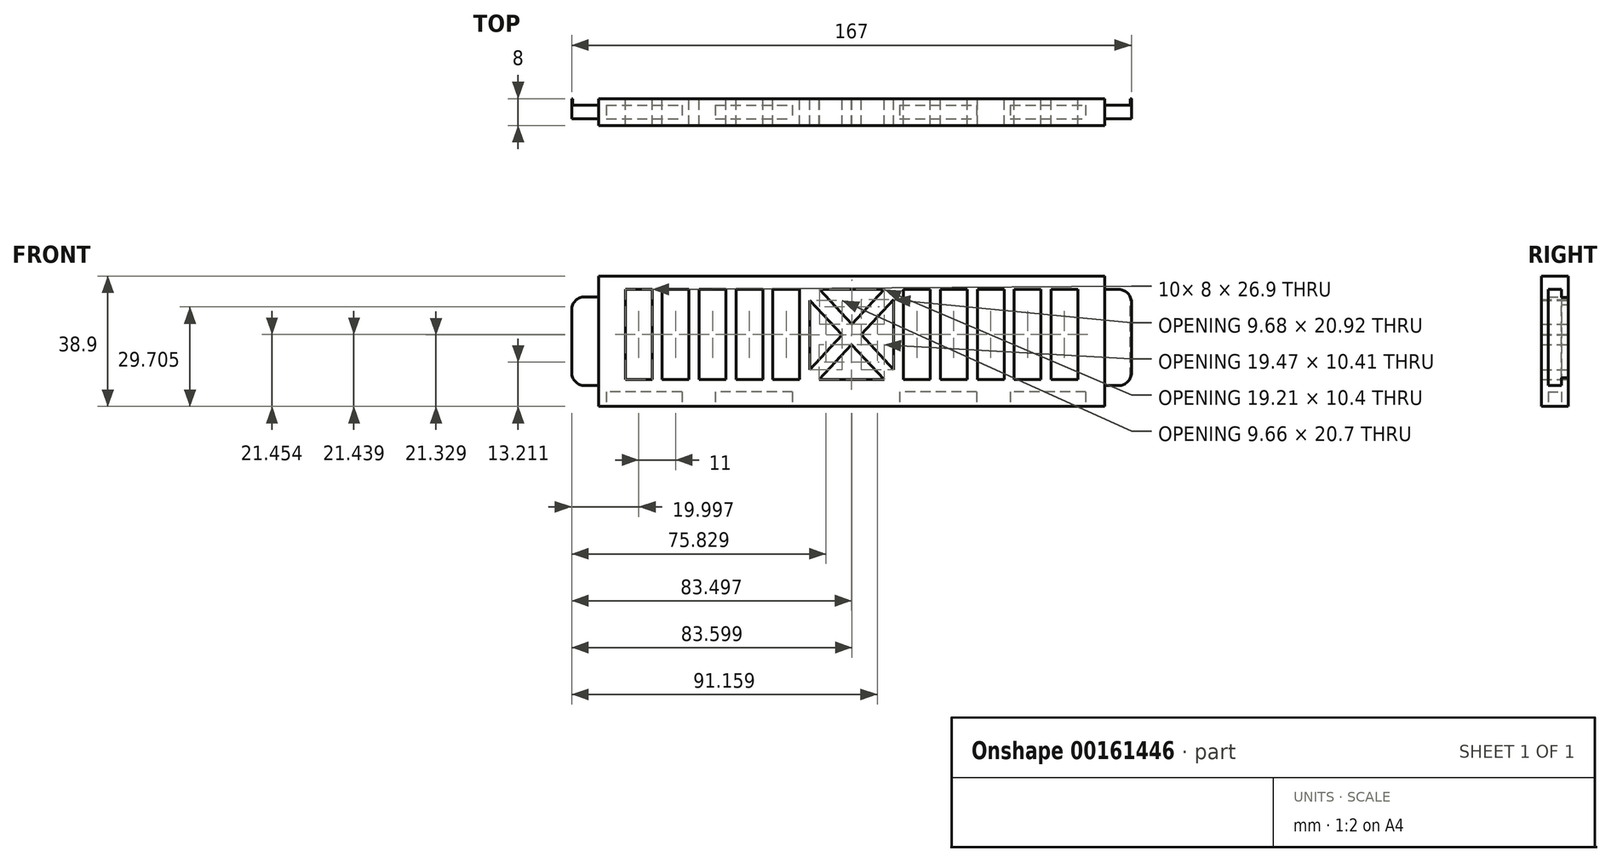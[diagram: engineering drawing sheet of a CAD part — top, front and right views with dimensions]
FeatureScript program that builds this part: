
annotation { "Feature Type Name" : "Feature", "Feature Type Description" : "" }
export const myFeature = defineFeature(function(context is Context, id is Id, definition is map)
    precondition{}
    {
        {
            var Q0;
            Q0=qCreatedBy(makeId("Front.planeOp"),FACE);
            var sketch = newSketch(context, id + "F0", { "sketchPlane" : qUnion([Q0])});
            skLineSegment(sketch, "E0.bottom", {"start": v(-77.72, 39.57) * mm, "end": v(73.28, 39.57) * mm});
            skLineSegment(sketch, "E0.top", {"start": v(-77.72, 0.67) * mm, "end": v(73.28, 0.67) * mm});
            skLineSegment(sketch, "E0.left", {"start": v(-77.72, 39.57) * mm, "end": v(-77.72, 0.67) * mm});
            skLineSegment(sketch, "E0.right", {"start": v(73.28, 39.57) * mm, "end": v(73.28, 0.67) * mm});
            skLineSegment(sketch, "E1.left", {"start": v(-77.72, 0.67) * mm, "end": v(-77.72, 15.56) * mm});
            skLineSegment(sketch, "E1.right", {"start": v(-85.72, 10.7) * mm, "end": v(-85.72, 29.54) * mm});
            skLineSegment(sketch, "E2.left", {"start": v(73.28, 39.57) * mm, "end": v(73.28, -23.35) * mm});
            skLineSegment(sketch, "E3.top", {"start": v(-77.72, 6.87) * mm, "end": v(-81.89, 6.87) * mm});
            skLineSegment(sketch, "E3.left", {"start": v(-77.72, 0.67) * mm, "end": v(-77.72, 6.87) * mm});
            skLineSegment(sketch, "E4.top", {"start": v(-81.89, 33.37) * mm, "end": v(-77.72, 33.37) * mm});
            skLineSegment(sketch, "E4.right", {"start": v(-77.72, 33.37) * mm, "end": v(-77.72, 15.56) * mm});
            skLineSegment(sketch, "E5.bottom", {"start": v(73.28, 6.87) * mm, "end": v(77.44, 6.87) * mm});
            skLineSegment(sketch, "E5.top", {"start": v(73.28, 35.57) * mm, "end": v(77.44, 35.57) * mm});
            skLineSegment(sketch, "E5.left", {"start": v(73.28, 6.87) * mm, "end": v(73.28, 35.57) * mm});
            skLineSegment(sketch, "E5.right", {"start": v(81.28, 10.7) * mm, "end": v(81.28, 31.74) * mm});
            skArc(sketch, "E6.filletArc", {"start": v(81.28, 31.74) * mm, "mid": v(80.15, 34.45) * mm, "end": v(77.44, 35.57) * mm});
            skPoint(sketch, "E7.visualSharp", {"position": v(81.28, 6.87) * mm});
            skArc(sketch, "E7.filletArc", {"start": v(77.44, 6.87) * mm, "mid": v(80.15, 8) * mm, "end": v(81.28, 10.7) * mm});
            skArc(sketch, "E8.filletArc", {"start": v(-81.89, 33.37) * mm, "mid": v(-84.6, 32.25) * mm, "end": v(-85.72, 29.54) * mm});
            skPoint(sketch, "E9.visualSharp", {"position": v(-85.72, 6.87) * mm});
            skArc(sketch, "E9.filletArc", {"start": v(-85.72, 10.7) * mm, "mid": v(-84.6, 8) * mm, "end": v(-81.89, 6.87) * mm});
            skLineSegment(sketch, "E10.bottom", {"start": v(-77.72, 39.57) * mm, "end": v(-69.72, 39.57) * mm});
            skLineSegment(sketch, "E10.top", {"start": v(-77.72, 0.67) * mm, "end": v(-69.72, 0.67) * mm});
            skLineSegment(sketch, "E10.right", {"start": v(-69.72, 35.57) * mm, "end": v(-69.72, 8.67) * mm});
            skLineSegment(sketch, "E11.bottom", {"start": v(73.28, 39.57) * mm, "end": v(65.28, 39.57) * mm});
            skLineSegment(sketch, "E11.top", {"start": v(73.28, 0.67) * mm, "end": v(65.28, 0.67) * mm});
            skLineSegment(sketch, "E11.right", {"start": v(65.28, 35.57) * mm, "end": v(65.28, 8.67) * mm});
            skLineSegment(sketch, "E12.bottom", {"start": v(-69.72, 8.67) * mm, "end": v(-61.72, 8.67) * mm});
            skLineSegment(sketch, "E12.left", {"start": v(-77.72, 8.67) * mm, "end": v(-77.72, 0.67) * mm});
            skLineSegment(sketch, "E12.right", {"start": v(73.28, 8.67) * mm, "end": v(73.28, 0.67) * mm});
            skLineSegment(sketch, "E13.top", {"start": v(-69.72, 35.57) * mm, "end": v(-61.72, 35.57) * mm});
            skLineSegment(sketch, "E13.left", {"start": v(-77.72, 39.57) * mm, "end": v(-77.72, 35.57) * mm});
            skLineSegment(sketch, "E13.right", {"start": v(73.28, 39.57) * mm, "end": v(73.28, 35.57) * mm});
            skLineSegment(sketch, "E14", {"start": v(-61.72, 35.57) * mm, "end": v(-61.72, 8.67) * mm});
            skLineSegment(sketch, "E15", {"start": v(-58.72, 35.57) * mm, "end": v(-58.72, 8.67) * mm});
            skLineSegment(sketch, "E16", {"start": v(-50.72, 35.57) * mm, "end": v(-50.72, 8.67) * mm});
            skLineSegment(sketch, "E17", {"start": v(-47.72, 35.57) * mm, "end": v(-47.72, 8.67) * mm});
            skLineSegment(sketch, "E18", {"start": v(-39.72, 35.57) * mm, "end": v(-39.72, 8.67) * mm});
            skLineSegment(sketch, "E19.bottom", {"start": v(-36.72, 35.57) * mm, "end": v(-28.72, 35.57) * mm});
            skLineSegment(sketch, "E19.top", {"start": v(-36.72, 8.67) * mm, "end": v(-28.72, 8.67) * mm});
            skLineSegment(sketch, "E19.left", {"start": v(-36.72, 35.57) * mm, "end": v(-36.72, 8.67) * mm});
            skLineSegment(sketch, "E19.right", {"start": v(-28.72, 35.57) * mm, "end": v(-28.72, 8.67) * mm});
            skLineSegment(sketch, "E20.bottom", {"start": v(-25.72, 35.57) * mm, "end": v(-17.72, 35.57) * mm});
            skLineSegment(sketch, "E20.top", {"start": v(-25.72, 8.67) * mm, "end": v(-17.72, 8.67) * mm});
            skLineSegment(sketch, "E20.left", {"start": v(-25.72, 35.57) * mm, "end": v(-25.72, 8.67) * mm});
            skLineSegment(sketch, "E20.right", {"start": v(-17.72, 35.57) * mm, "end": v(-17.72, 8.67) * mm});
            skLineSegment(sketch, "E21.left", {"start": v(-14.72, 32.35) * mm, "end": v(-14.72, 11.65) * mm});
            skLineSegment(sketch, "E22.left", {"start": v(10.28, 32.57) * mm, "end": v(10.28, 11.65) * mm});
            skLineSegment(sketch, "E22.right", {"start": v(13.28, 35.57) * mm, "end": v(13.28, 8.67) * mm});
            skLineSegment(sketch, "E23.left", {"start": v(21.28, 35.57) * mm, "end": v(21.28, 8.67) * mm});
            skLineSegment(sketch, "E23.right", {"start": v(24.28, 35.57) * mm, "end": v(24.28, 8.67) * mm});
            skLineSegment(sketch, "E24.bottom", {"start": v(32.28, 35.57) * mm, "end": v(35.28, 35.57) * mm});
            skLineSegment(sketch, "E24.left", {"start": v(32.28, 35.57) * mm, "end": v(32.28, 8.67) * mm});
            skLineSegment(sketch, "E24.right", {"start": v(35.28, 35.57) * mm, "end": v(35.28, 8.67) * mm});
            skLineSegment(sketch, "E25.left", {"start": v(43.28, 35.57) * mm, "end": v(43.28, 8.67) * mm});
            skLineSegment(sketch, "E25.right", {"start": v(46.28, 35.57) * mm, "end": v(46.28, 8.67) * mm});
            skLineSegment(sketch, "E26.left", {"start": v(54.28, 35.57) * mm, "end": v(54.28, 8.67) * mm});
            skLineSegment(sketch, "E26.right", {"start": v(57.28, 35.57) * mm, "end": v(57.28, 8.67) * mm});
            skLineSegment(sketch, "E27.right", {"start": v(73.28, 11.56) * mm, "end": v(73.28, 8.67) * mm});
            skPoint(sketch, "E28.start.orphan", {"position": v(65.28, 24.02) * mm});
            skLineSegment(sketch, "E29", {"start": v(10.28, 32.57) * mm, "end": v(0.6, 22.17) * mm});
            skLineSegment(sketch, "E30", {"start": v(-14.72, 11.65) * mm, "end": v(-5.06, 22.06) * mm});
            skLineSegment(sketch, "E31", {"start": v(10.28, 11.65) * mm, "end": v(0.6, 22.17) * mm});
            skLineSegment(sketch, "E32", {"start": v(-14.72, 32.35) * mm, "end": v(-5.06, 22.06) * mm});
            skLineSegment(sketch, "E33.trimOffspring", {"start": v(13.28, 35.57) * mm, "end": v(21.28, 35.57) * mm});
            skLineSegment(sketch, "E34.trimOffspring", {"start": v(-2.17, 25.18) * mm, "end": v(-11.73, 35.57) * mm});
            skLineSegment(sketch, "E35.trimOffspring", {"start": v(-2.27, 19.09) * mm, "end": v(-11.96, 8.67) * mm});
            skLineSegment(sketch, "E36.trimOffspring", {"start": v(-2.17, 25.18) * mm, "end": v(7.48, 35.57) * mm});
            skLineSegment(sketch, "E37.trimOffspring", {"start": v(-2.27, 19.09) * mm, "end": v(7.51, 8.67) * mm});
            skLineSegment(sketch, "E38.trimOffspring", {"start": v(13.28, 8.67) * mm, "end": v(21.28, 8.67) * mm});
            skLineSegment(sketch, "E39.trimOffspring", {"start": v(24.28, 8.67) * mm, "end": v(32.28, 8.67) * mm});
            skLineSegment(sketch, "E40.trimOffspring", {"start": v(35.28, 8.67) * mm, "end": v(43.28, 8.67) * mm});
            skLineSegment(sketch, "E41.trimOffspring", {"start": v(57.28, 8.67) * mm, "end": v(65.28, 8.67) * mm});
            skLineSegment(sketch, "E42.trimOffspring", {"start": v(24.28, 35.57) * mm, "end": v(32.28, 35.57) * mm});
            skLineSegment(sketch, "E43.trimOffspring", {"start": v(35.28, 35.57) * mm, "end": v(43.28, 35.57) * mm});
            skLineSegment(sketch, "E44.trimOffspring", {"start": v(46.28, 35.57) * mm, "end": v(54.28, 35.57) * mm});
            skLineSegment(sketch, "E45.trimOffspring", {"start": v(-47.72, 35.57) * mm, "end": v(-39.72, 35.57) * mm});
            skLineSegment(sketch, "E46.trimOffspring", {"start": v(-58.72, 8.67) * mm, "end": v(-50.72, 8.67) * mm});
            skLineSegment(sketch, "E47.trimOffspring", {"start": v(-58.72, 35.57) * mm, "end": v(-50.72, 35.57) * mm});
            skLineSegment(sketch, "E48.trimOffspring", {"start": v(-47.72, 8.67) * mm, "end": v(-39.72, 8.67) * mm});
            skLineSegment(sketch, "E49.trimOffspring", {"start": v(57.28, 35.57) * mm, "end": v(65.28, 35.57) * mm});
            skLineSegment(sketch, "E50.trimOffspring", {"start": v(46.28, 8.67) * mm, "end": v(54.28, 8.67) * mm});
            skLineSegment(sketch, "E51", {"start": v(80.98, 9.22) * mm, "end": v(80.98, 33.23) * mm});
            skLineSegment(sketch, "E52", {"start": v(-85.42, 9.22) * mm, "end": v(-85.42, 31.03) * mm});
            skLineSegment(sketch, "E53", {"start": v(-11.73, 35.57) * mm, "end": v(7.48, 35.57) * mm});
            skLineSegment(sketch, "E54", {"start": v(7.51, 8.67) * mm, "end": v(-11.96, 8.67) * mm});
            skSolve(sketch);
        }
        {
            var Q0;
            {var subQ4=sQuery(id+"F0.wireOp",EDGE,"E1.right");Q0=makeQuery(id+"F0.imprint","IMPRINT",FACE,{"disambiguationData":[TD([[makeQuery(id+"F0.imprint","IMPRINT",EDGE,{"derivedFrom":subQ4}),-1.0]])]});}
            var Q1;
            {var subQ1=sQuery(id+"F0.wireOp",EDGE,"E5.right");Q1=makeQuery(id+"F0.imprint","IMPRINT",FACE,{"disambiguationData":[TD([[makeQuery(id+"F0.imprint","IMPRINT",EDGE,{"derivedFrom":subQ1}),1.0]])]});}
            var Q2;
            {var subQ1=sQuery(id+"F0.wireOp",EDGE,"E5.bottom");Q2=makeQuery(id+"F0.imprint","IMPRINT",FACE,{"disambiguationData":[TD([[makeQuery(id+"F0.imprint","IMPRINT",EDGE,{"derivedFrom":subQ1}),1.0]])]});}
            var Q3;
            Q3=makeQuery(id+"F0.imprint","IMPRINT",FACE,{"disambiguationData":[TD([[makeQuery(id+"F0.imprint","IMPRINT",EDGE,{"derivedFrom":sQuery(id+"F0.wireOp",EDGE,"E10.right")}),-1.0]])]});
            var Q4;
            {var subQ1=sQuery(id+"F0.wireOp",EDGE,"E3.top");Q4=makeQuery(id+"F0.imprint","IMPRINT",FACE,{"disambiguationData":[TD([[makeQuery(id+"F0.imprint","IMPRINT",EDGE,{"derivedFrom":subQ1}),-1.0]])]});}
            extrude(context, id + "F1", {"entities" : qUnion([Q0, Q1, Q2, Q3, Q4]), "depth" : 6 * mm});
        }
        {
            var Q0;
            {var subQ1=sQuery(id+"F0.wireOp",EDGE,"E3.top");Q0=makeQuery(id+"F0.imprint","IMPRINT",FACE,{"disambiguationData":[TD([[makeQuery(id+"F0.imprint","IMPRINT",EDGE,{"derivedFrom":subQ1}),-1.0]])]});}
            var Q1;
            {var subQ1=sQuery(id+"F0.wireOp",EDGE,"E5.bottom");Q1=makeQuery(id+"F0.imprint","IMPRINT",FACE,{"disambiguationData":[TD([[makeQuery(id+"F0.imprint","IMPRINT",EDGE,{"derivedFrom":subQ1}),1.0]])]});}
            extrude(context, id + "F2", {"entities" : qUnion([Q0, Q1]), "operationType" : NewBodyOperationType.REMOVE, "depth" : 2 * mm});
        }
        {
            var Q0;
            Q0=makeQuery(id+"F0.imprint","IMPRINT",FACE,{"disambiguationData":[TD([[makeQuery(id+"F0.imprint","IMPRINT",EDGE,{"derivedFrom":sQuery(id+"F0.wireOp",EDGE,"E10.right")}),-1.0]])]});
            extrude(context, id + "F3", {"entities" : qUnion([Q0]), "operationType" : NewBodyOperationType.ADD, "depth" : 8 * mm});
        }
        {
            var Q0;
            Q0=qCreatedBy(makeId("Top.planeOp"),FACE);
            var sketch = newSketch(context, id + "F4", { "sketchPlane" : qUnion([Q0])});
            skLineSegment(sketch, "E55.bottom", {"start": v(67.63, -6) * mm, "end": v(12.13, -6) * mm});
            skLineSegment(sketch, "E55.top", {"start": v(67.63, -2) * mm, "end": v(12.13, -2) * mm});
            skLineSegment(sketch, "E55.left", {"start": v(67.63, -6) * mm, "end": v(67.63, -2) * mm});
            skLineSegment(sketch, "E55.right", {"start": v(-75.37, -6) * mm, "end": v(-75.37, -2) * mm});
            skLineSegment(sketch, "E56", {"start": v(45.13, -6) * mm, "end": v(45.13, -2) * mm});
            skLineSegment(sketch, "E57", {"start": v(-52.87, -6) * mm, "end": v(-52.87, -2) * mm});
            skLineSegment(sketch, "E58", {"start": v(-52.87, -2) * mm, "end": v(-52.87, -4) * mm});
            skLineSegment(sketch, "E59", {"start": v(-42.87, -6) * mm, "end": v(-42.87, -2) * mm});
            skLineSegment(sketch, "E60", {"start": v(35.13, -6) * mm, "end": v(35.13, -2) * mm});
            skLineSegment(sketch, "E61", {"start": v(12.13, -6) * mm, "end": v(12.13, -2) * mm});
            skLineSegment(sketch, "E62", {"start": v(-19.87, -6) * mm, "end": v(-19.87, -2) * mm});
            skLineSegment(sketch, "E63", {"start": v(-19.87, -2) * mm, "end": v(-19.87, -4) * mm});
            skLineSegment(sketch, "E64.trimOffspring", {"start": v(-19.87, -6) * mm, "end": v(-75.37, -6) * mm});
            skLineSegment(sketch, "E65.trimOffspring", {"start": v(-19.87, -2) * mm, "end": v(-75.37, -2) * mm});
            skSolve(sketch);
        }
        {
            var Q0;
            {var subQ3=sQuery(id+"F4.wireOp",EDGE,"E55.right");Q0=makeQuery(id+"F4.imprint","IMPRINT",FACE,{"disambiguationData":[TD([[makeQuery(id+"F4.imprint","IMPRINT",EDGE,{"derivedFrom":subQ3}),-1.0]])]});}
            var Q1;
            {var subQ1=sQuery(id+"F4.wireOp",EDGE,"E59");Q1=makeQuery(id+"F4.imprint","IMPRINT",FACE,{"disambiguationData":[TD([[makeQuery(id+"F4.imprint","IMPRINT",EDGE,{"derivedFrom":subQ1}),-1.0]])]});}
            var Q2;
            {var subQ2=sQuery(id+"F4.wireOp",EDGE,"E60");Q2=makeQuery(id+"F4.imprint","IMPRINT",FACE,{"disambiguationData":[TD([[makeQuery(id+"F4.imprint","IMPRINT",EDGE,{"derivedFrom":subQ2}),1.0]])]});}
            var Q3;
            {var subQ0=sQuery(id+"F4.wireOp",EDGE,"E55.left");Q3=makeQuery(id+"F4.imprint","IMPRINT",FACE,{"disambiguationData":[TD([[makeQuery(id+"F4.imprint","IMPRINT",EDGE,{"derivedFrom":subQ0}),1.0]])]});}
            extrude(context, id + "F5", {"entities" : qUnion([Q0, Q1, Q2, Q3]), "operationType" : NewBodyOperationType.REMOVE, "depth" : 5 * mm});
        }
    });
